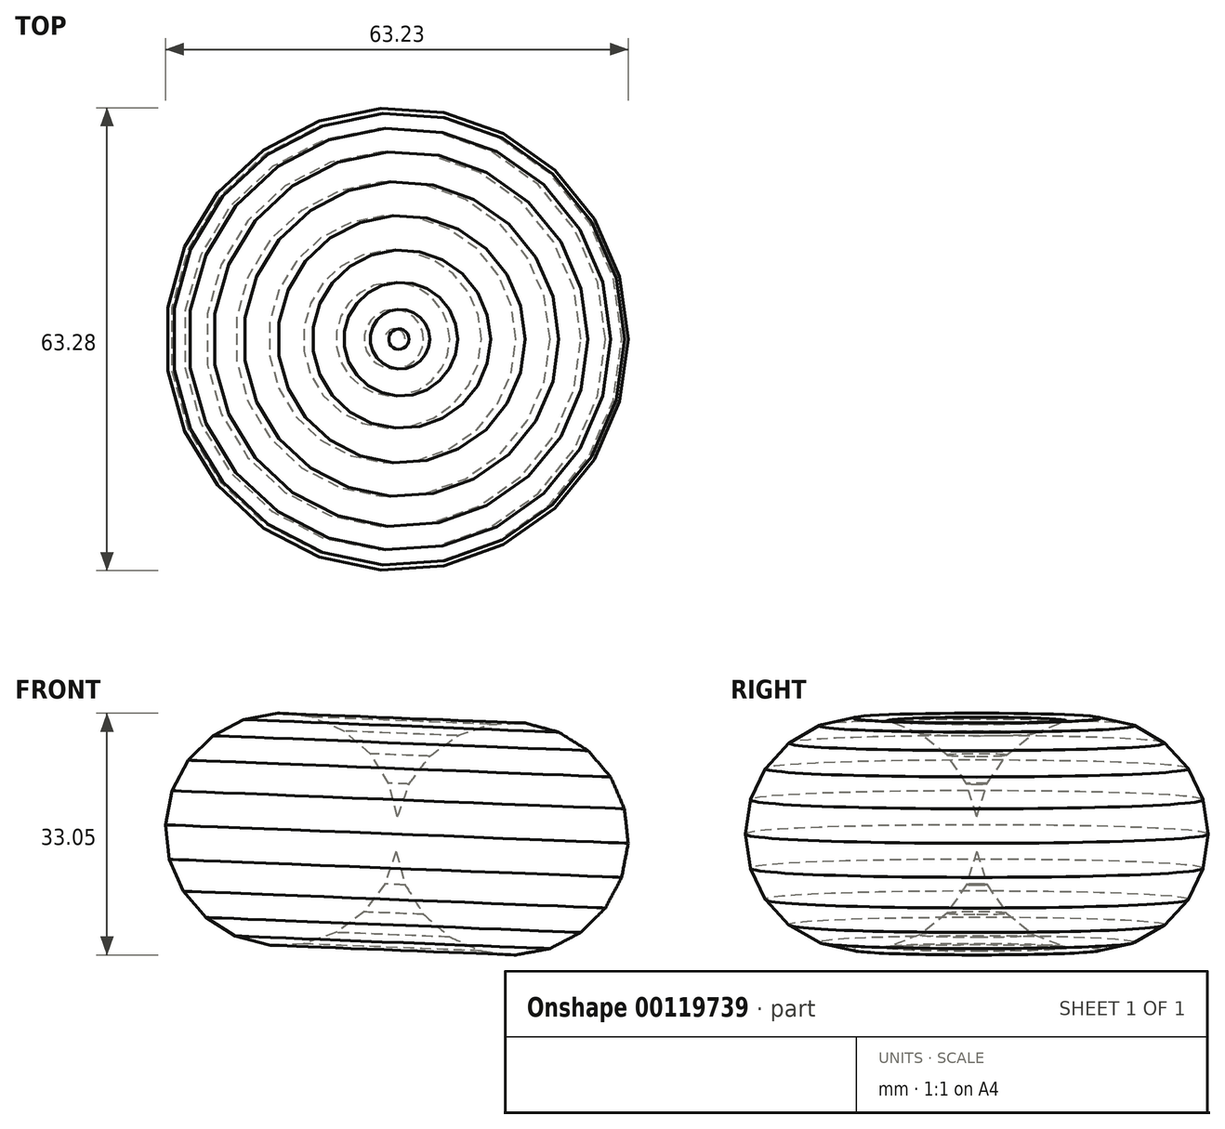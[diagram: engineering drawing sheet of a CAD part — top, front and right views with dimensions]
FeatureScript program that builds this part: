
annotation { "Feature Type Name" : "Feature", "Feature Type Description" : "" }
export const myFeature = defineFeature(function(context is Context, id is Id, definition is map)
    precondition{}
    {
        {
            var Q0;
            Q0=qCreatedBy(makeId("Front.planeOp"),FACE);
            var sketch = newSketch(context, id + "F0", { "sketchPlane" : qUnion([Q0])});
            skCircle(sketch, "E0.cCircle", {"center": v(-16.02, 0) * mm, "radius": 15.73 * mm, "construction": true});
            skLineSegment(sketch, "E0.0", {"start": v(-17.84, -15.8) * mm, "end": v(-22.42, -14.56) * mm});
            skLineSegment(sketch, "E0.1", {"start": v(-22.42, -14.56) * mm, "end": v(-26.43, -12.03) * mm});
            skLineSegment(sketch, "E0.2", {"start": v(-26.43, -12.03) * mm, "end": v(-29.51, -8.43) * mm});
            skLineSegment(sketch, "E0.3", {"start": v(-29.51, -8.43) * mm, "end": v(-31.4, -4.08) * mm});
            skLineSegment(sketch, "E0.4", {"start": v(-31.4, -4.08) * mm, "end": v(-31.92, 0.63) * mm});
            skLineSegment(sketch, "E0.5", {"start": v(-31.92, 0.63) * mm, "end": v(-31.03, 5.3) * mm});
            skLineSegment(sketch, "E0.6", {"start": v(-31.03, 5.3) * mm, "end": v(-28.8, 9.48) * mm});
            skLineSegment(sketch, "E0.7", {"start": v(-28.8, 9.48) * mm, "end": v(-25.44, 12.82) * mm});
            skLineSegment(sketch, "E0.8", {"start": v(-25.44, 12.82) * mm, "end": v(-21.24, 15.03) * mm});
            skLineSegment(sketch, "E0.9", {"start": v(-21.24, 15.03) * mm, "end": v(-16.58, 15.9) * mm});
            skLineSegment(sketch, "E0.10", {"start": v(-16.58, 15.9) * mm, "end": v(-11.87, 15.36) * mm});
            skLineSegment(sketch, "E0.11", {"start": v(-11.87, 15.36) * mm, "end": v(-7.53, 13.45) * mm});
            skLineSegment(sketch, "E0.12", {"start": v(-7.53, 13.45) * mm, "end": v(-3.94, 10.35) * mm});
            skLineSegment(sketch, "E0.13", {"start": v(-3.94, 10.35) * mm, "end": v(-1.43, 6.33) * mm});
            skLineSegment(sketch, "E0.14", {"start": v(-1.43, 6.33) * mm, "end": v(-0.21, 1.74) * mm});
            skLineSegment(sketch, "E0.15", {"start": v(-0.21, 1.74) * mm, "end": v(-0.4, -3) * mm});
            skLineSegment(sketch, "E0.16", {"start": v(-0.4, -3) * mm, "end": v(-1.98, -7.47) * mm});
            skLineSegment(sketch, "E0.17", {"start": v(-1.98, -7.47) * mm, "end": v(-4.8, -11.28) * mm});
            skLineSegment(sketch, "E0.18", {"start": v(-4.8, -11.28) * mm, "end": v(-8.63, -14.08) * mm});
            skLineSegment(sketch, "E0.19", {"start": v(-8.63, -14.08) * mm, "end": v(-13.1, -15.64) * mm});
            skLineSegment(sketch, "E0.20", {"start": v(-13.1, -15.64) * mm, "end": v(-17.84, -15.8) * mm});
            skPoint(sketch, "E0.0.midPoint", {"position": v(-20.13, -15.18) * mm});
            skSolve(sketch);
        }
        {
            var Q0;
            Q0 = qSketchRegion(id + "F0", true);
            var Q1;
            Q1=sQuery(id+"F0.wireOp",EDGE,"E0.15");
            revolve(context, id + "F1", {"entities" : qUnion([Q0]), "axis" : qUnion([Q1]), "revolveType" : RevolveType.FULL});
        }
    });
